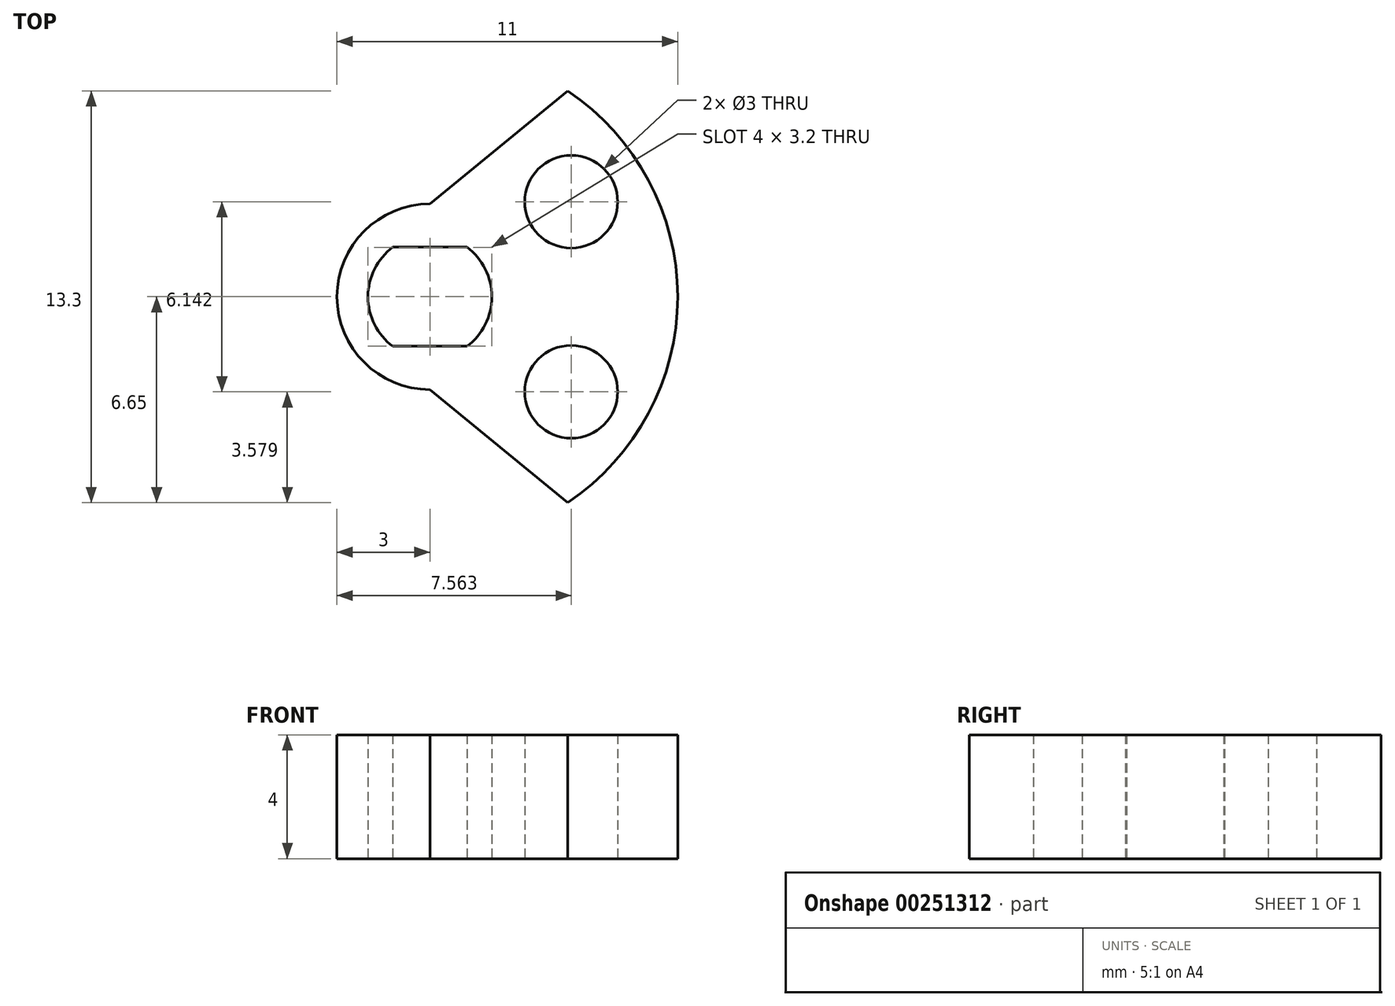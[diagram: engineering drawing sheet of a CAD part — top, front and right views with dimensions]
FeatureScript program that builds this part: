
annotation { "Feature Type Name" : "Feature", "Feature Type Description" : "" }
export const myFeature = defineFeature(function(context is Context, id is Id, definition is map)
    precondition{}
    {
        {
            var Q0;
            Q0=qCreatedBy(makeId("Top.planeOp"),FACE);
            var sketch = newSketch(context, id + "F0", { "sketchPlane" : qUnion([Q0])});
            skArc(sketch, "E0", {"start": v(1.2, -1.6) * mm, "mid": v(2, 0) * mm, "end": v(1.2, 1.6) * mm});
            skCircle(sketch, "E1.0", {"center": v(0, 0) * mm, "radius": 3 * mm});
            skArc(sketch, "E2", {"start": v(4.45, -6.65) * mm, "mid": v(8, 0) * mm, "end": v(4.45, 6.65) * mm});
            skLineSegment(sketch, "E3", {"start": v(0, 8) * mm, "end": v(0, -8.04) * mm, "construction": true});
            skLineSegment(sketch, "E4", {"start": v(0, 3) * mm, "end": v(4.45, 6.65) * mm});
            skLineSegment(sketch, "E5", {"start": v(0, 0) * mm, "end": v(10.48, 0) * mm, "construction": true});
            skLineSegment(sketch, "E6.MirrorCS", {"start": v(0, -3) * mm, "end": v(4.45, -6.65) * mm});
            skCircle(sketch, "E7", {"center": v(4.56, 3.07) * mm, "radius": 1.5 * mm});
            skCircle(sketch, "E8.MirrorC", {"center": v(4.56, -3.07) * mm, "radius": 1.5 * mm});
            skLineSegment(sketch, "E9.bottom", {"start": v(1.2, 1.6) * mm, "end": v(-1.2, 1.6) * mm});
            skLineSegment(sketch, "E9.top", {"start": v(1.2, -1.6) * mm, "end": v(-1.2, -1.6) * mm});
            skArc(sketch, "E10.trimOffspring", {"start": v(-1.2, 1.6) * mm, "mid": v(-2, 0) * mm, "end": v(-1.2, -1.6) * mm});
            skSolve(sketch);
        }
        {
            var Q0;
            Q0=makeQuery(id+"F0.imprint","IMPRINT",FACE,{"disambiguationData":[TD([[makeQuery(id+"F0.imprint","IMPRINT",EDGE,{"derivedFrom":sQuery(id+"F0.wireOp",EDGE,"E2")}),1.0]])]});
            var Q1;
            Q1=makeQuery(id+"F0.imprint","IMPRINT",FACE,{"disambiguationData":[TD([[makeQuery(id+"F0.imprint","IMPRINT",EDGE,{"derivedFrom":sQuery(id+"F0.wireOp",EDGE,"E0")}),-1.0]])]});
            extrude(context, id + "F1", {"entities" : qUnion([Q0, Q1]), "depth" : 4 * mm, "offsetDistance" : 25 * mm});
        }
    });
